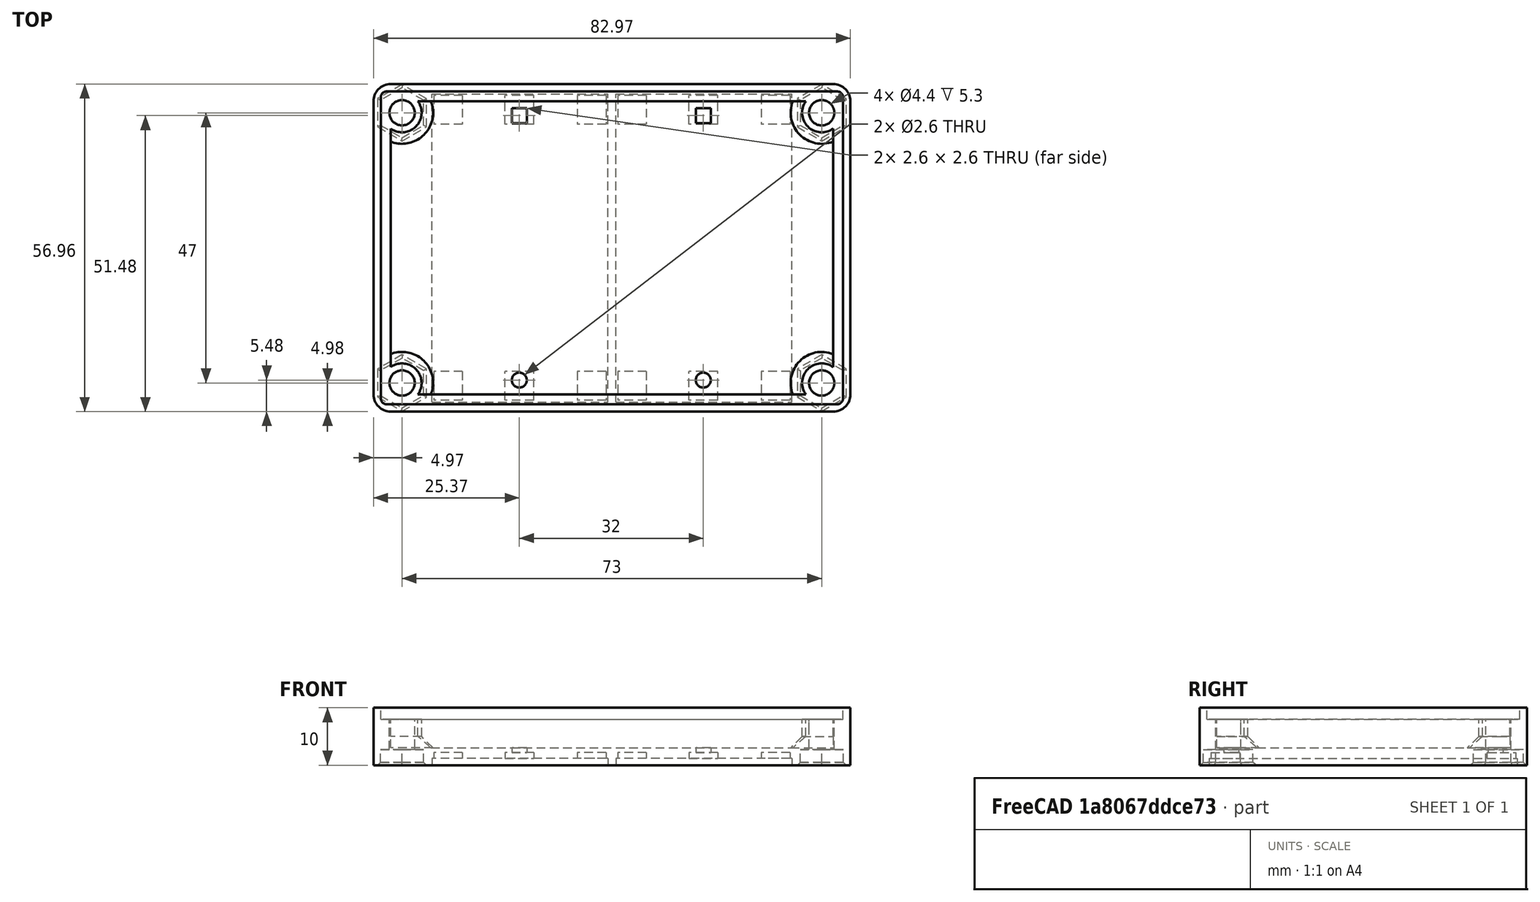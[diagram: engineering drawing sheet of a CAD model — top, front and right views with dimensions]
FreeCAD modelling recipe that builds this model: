
FCSTD DOCUMENT  (FreeCAD 0.18.4R)
Label: DoubleSolarPlate3
License: All rights reserved
LicenseURL: http://en.wikipedia.org/wiki/All_rights_reserved
objects: Part::Box×21, Part::Cylinder×14, Part::Cut×9, Part::MultiFuse×7, Sketcher::SketchObject×5, PartDesign::Pad×5, Part::Chamfer×2, Part::Fillet×1, Mesh::Feature×1
note: 69 computed .brp shape members not serialized (recipe doc carries the construction recipe); baked Part::Feature solids carry a one-line shape summary decoded from their .brp

FEATURE [Sketcher::SketchObject] Sketch002
  MapMode = 5
  sketch-geometry (8):
    g0: LineSegment StartX=7.02468 StartY=-27.9753 StartZ=0 EndX=-69.9815 EndY=-27.9753 EndZ=0
    g1: LineSegment StartX=-72.9716 StartY=-24.9853 StartZ=0 EndX=-72.9716 EndY=25.9942 EndZ=0
    g2: LineSegment StartX=-69.9853 StartY=28.9804 StartZ=0 EndX=7.02249 EndY=28.9804 EndZ=0
    g3: LineSegment StartX=10 StartY=26.0029 StartZ=0 EndX=10 EndY=-25 EndZ=0
    g4: ArcOfCircle CenterX=7.02468 CenterY=-25 CenterZ=0 NormalX=0 NormalY=0 NormalZ=1 AngleXU=0 Radius=2.97532 StartAngle=4.71239 EndAngle=6.28319
    g5: ArcOfCircle CenterX=-69.9815 CenterY=-24.9853 CenterZ=0 NormalX=0 NormalY=0 NormalZ=1 AngleXU=0 Radius=2.99005 StartAngle=3.14159 EndAngle=4.71239
    g6: ArcOfCircle CenterX=-69.9853 CenterY=25.9942 CenterZ=0 NormalX=0 NormalY=0 NormalZ=1 AngleXU=0 Radius=2.98622 StartAngle=1.5708 EndAngle=3.14159
    g7: ArcOfCircle CenterX=7.02249 CenterY=26.0029 CenterZ=0 NormalX=0 NormalY=0 NormalZ=1 AngleXU=0 Radius=2.97751 StartAngle=1.036e-13 EndAngle=1.5708
  constraints (12):
    c: Horizontal(g0)
    c: Horizontal(g2)
    c: Vertical(g1)
    c: Vertical(g3)
    c: Tangent(g3,g4) = 1.5708
    c: Tangent(g0,g4) = 1.5708
    c: Tangent(g1,g5) = 1.5708
    c: Tangent(g0,g5) = 1.5708
    c: Tangent(g1,g6) = 1.5708
    c: Tangent(g2,g6) = 1.5708
    c: Tangent(g2,g7) = 1.5708
    c: Tangent(g3,g7) = 1.5708
FEATURE [PartDesign::Pad] Pad013
  Length = 10
  Length2 = 100
  Profile = -> Sketch002
  Type = 0
FEATURE [Part::Box] Box010  label="Würfel010"
  AttacherType = Attacher::AttachEngine3D
  Height = 25
  Length = 77
  Placement = pos=(-70,-25,3) rot=(0,0,1;0rad)
  Width = 51
FEATURE [Part::Cut] Cut011
  Base = -> Pad013
  Tool = -> Box010
FEATURE [Part::Box] Box  label="Rand002"
  AttacherType = Attacher::AttachEngine3D
  Height = 2
  Length = 80.4
  Placement = pos=(-71.7,25.7,14) rot=(0,0,1;0rad)
  Width = 2
FEATURE [Part::Box] Box011  label="Rand001"
  AttacherType = Attacher::AttachEngine3D
  Height = 2
  Length = 80.4
  Placement = pos=(-71.7,-26.7,14) rot=(0,0,1;0rad)
  Width = 2
FEATURE [Part::Box] Box012  label="Rand003"
  AttacherType = Attacher::AttachEngine3D
  Height = 2
  Length = 2
  Placement = pos=(-71.7,-25,14) rot=(0,0,1;0rad)
  Width = 51
FEATURE [Part::Box] Box013  label="Rand004"
  AttacherType = Attacher::AttachEngine3D
  Height = 2
  Length = 2
  Placement = pos=(6.7,-25,14) rot=(0,0,1;0rad)
  Width = 51
FEATURE [Part::MultiFuse] Fusion  label="RandFraesung"
  Placement = pos=(0,0,-6) rot=(0,0,1;0rad)
  Shapes = -> [Box013,Box012,Box011,Box]
FEATURE [Part::Cut] Cut  label="DeckelRaw"
  Base = -> Cut011
  Tool = -> Fusion
FEATURE [Part::Cylinder] Cylinder004  label="Zylinder002"
  Angle = 360
  AttacherType = Attacher::AttachEngine3D
  Height = 8
  Radius = 3.4
FEATURE [Part::Cylinder] Cylinder  label="Zylinder001"
  Angle = 360
  AttacherType = Attacher::AttachEngine3D
  Height = 6
  Radius = 2.2
FEATURE [Part::Cut] Cut027  label="Dom001"
  Base = -> Cylinder004
  Placement = pos=(5,-23,0) rot=(0,0,1;0rad)
  Tool = -> Cylinder
FEATURE [Part::Cylinder] Cylinder015  label="Zylinder015"
  Angle = 360
  AttacherType = Attacher::AttachEngine3D
  Height = 8
  Radius = 3.4
FEATURE [Part::Cylinder] Cylinder016  label="Zylinder016"
  Angle = 360
  AttacherType = Attacher::AttachEngine3D
  Height = 10
  Radius = 2.2
FEATURE [Part::Cut] Cut028  label="Dom002"
  Base = -> Cylinder015
  Placement = pos=(-68,-23,0) rot=(0,0,1;0rad)
  Tool = -> Cylinder016
FEATURE [Part::Cylinder] Cylinder017  label="Zylinder017"
  Angle = 360
  AttacherType = Attacher::AttachEngine3D
  Height = 8
  Radius = 3.4
FEATURE [Part::Cylinder] Cylinder018  label="Zylinder018"
  Angle = 360
  AttacherType = Attacher::AttachEngine3D
  Height = 10
  Radius = 2.2
FEATURE [Part::Cut] Cut029  label="Dom003"
  Base = -> Cylinder017
  Placement = pos=(-68,24,0) rot=(0,0,1;0rad)
  Tool = -> Cylinder018
FEATURE [Part::Cylinder] Cylinder019  label="Zylinder019"
  Angle = 360
  AttacherType = Attacher::AttachEngine3D
  Height = 8
  Radius = 3.4
FEATURE [Part::Cylinder] Cylinder020  label="Zylinder020"
  Angle = 360
  AttacherType = Attacher::AttachEngine3D
  Height = 10
  Radius = 2.2
FEATURE [Part::Cut] Cut030  label="Dom004"
  Base = -> Cylinder019
  Placement = pos=(5,24,0) rot=(0,0,1;0rad)
  Tool = -> Cylinder020
FEATURE [Part::MultiFuse] Fusion001  label="DeckelMitDomen"
  Shapes = -> [Cut,Cut027,Cut028,Cut029,Cut030]
FEATURE [Part::Cylinder] Cylinder021  label="DeckelBohrung001"
  Angle = 360
  AttacherType = Attacher::AttachEngine3D
  Height = 10
  Placement = pos=(5,-23,0) rot=(0,0,1;0rad)
  Radius = 2.2
FEATURE [Part::Cylinder] Cylinder022  label="DeckelBohrung002"
  Angle = 360
  AttacherType = Attacher::AttachEngine3D
  Height = 10
  Placement = pos=(-68,-23,0) rot=(0,0,1;0rad)
  Radius = 2.2
FEATURE [Part::Cylinder] Cylinder023  label="DeckelBohrung003"
  Angle = 360
  AttacherType = Attacher::AttachEngine3D
  Height = 10
  Placement = pos=(-68,24,0) rot=(0,0,1;0rad)
  Radius = 2.2
FEATURE [Part::Cylinder] Cylinder024  label="DeckelBohrung004"
  Angle = 360
  AttacherType = Attacher::AttachEngine3D
  Height = 10
  Placement = pos=(5,24,0) rot=(0,0,1;0rad)
  Radius = 2.2
FEATURE [Part::MultiFuse] Fusion002  label="DeckelBohrungen"
  Shapes = -> [Cylinder021,Cylinder022,Cylinder023,Cylinder024]
FEATURE [Part::Cut] Cut031  label="DomeDeckelGebohrt"
  Base = -> Fusion001
  Tool = -> Fusion002
FEATURE [Sketcher::SketchObject] Sketch001
  MapMode = 5
  Placement = pos=(5,-23,0) rot=(0,0,1;0.523599rad)
  sketch-geometry (7):
    g0: LineSegment StartX=4.32745 StartY=0.001167 StartZ=0 EndX=2.16272 EndY=3.74827 EndZ=0
    g1: LineSegment StartX=2.16272 StartY=3.74827 StartZ=0 EndX=-2.16474 EndY=3.7471 EndZ=0
    g2: LineSegment StartX=-2.16474 StartY=3.7471 StartZ=0 EndX=-4.32745 EndY=-0.001167 EndZ=0
    g3: LineSegment StartX=-4.32745 StartY=-0.001167 StartZ=0 EndX=-2.16272 EndY=-3.74827 EndZ=0
    g4: LineSegment StartX=-2.16272 StartY=-3.74827 StartZ=0 EndX=2.16474 EndY=-3.7471 EndZ=0
    g5: LineSegment StartX=2.16474 StartY=-3.7471 StartZ=0 EndX=4.32745 EndY=0.001167 EndZ=0
    g6: Circle [constr] CenterX=0 CenterY=0 CenterZ=0 NormalX=0 NormalY=0 NormalZ=1 AngleXU=0 Radius=4.32745
  constraints (13):
    c: Coincident(g0,g1)
    c: Coincident(g1,g2)
    c: Coincident(g2,g3)
    c: Coincident(g3,g4)
    c: Coincident(g4,g5)
    c: Coincident(g5,g0)
    c: Equal(g0, g1-g5) x5
    c: PointOnObject(g0,g6)
    c: PointOnObject(g1,g6)
    c: PointOnObject(g2,g6)
    c: PointOnObject(g3,g6)
    c: PointOnObject(g4,g6)
    c: PointOnObject(g5,g6)
FEATURE [PartDesign::Pad] Pad  label="ScrewNut001"
  Length = 2.7
  Length2 = 100
  Placement = pos=(5,-23,0) rot=(0,0,1;0.523599rad)
  Profile = -> Sketch001
  Type = 0
FEATURE [Sketcher::SketchObject] Sketch003
  MapMode = 5
  Placement = pos=(-68,-23,0) rot=(0,0,1;0.523599rad)
  sketch-geometry (7):
    g0: LineSegment StartX=4.32745 StartY=0.001167 StartZ=0 EndX=2.16272 EndY=3.74827 EndZ=0
    g1: LineSegment StartX=2.16272 StartY=3.74827 StartZ=0 EndX=-2.16474 EndY=3.7471 EndZ=0
    g2: LineSegment StartX=-2.16474 StartY=3.7471 StartZ=0 EndX=-4.32745 EndY=-0.001167 EndZ=0
    g3: LineSegment StartX=-4.32745 StartY=-0.001167 StartZ=0 EndX=-2.16272 EndY=-3.74827 EndZ=0
    g4: LineSegment StartX=-2.16272 StartY=-3.74827 StartZ=0 EndX=2.16474 EndY=-3.7471 EndZ=0
    g5: LineSegment StartX=2.16474 StartY=-3.7471 StartZ=0 EndX=4.32745 EndY=0.001167 EndZ=0
    g6: Circle [constr] CenterX=0 CenterY=0 CenterZ=0 NormalX=0 NormalY=0 NormalZ=1 AngleXU=0 Radius=4.32745
  constraints (13):
    c: Coincident(g0,g1)
    c: Coincident(g1,g2)
    c: Coincident(g2,g3)
    c: Coincident(g3,g4)
    c: Coincident(g4,g5)
    c: Coincident(g5,g0)
    c: Equal(g0, g1-g5) x5
    c: PointOnObject(g0,g6)
    c: PointOnObject(g1,g6)
    c: PointOnObject(g2,g6)
    c: PointOnObject(g3,g6)
    c: PointOnObject(g4,g6)
    c: PointOnObject(g5,g6)
FEATURE [PartDesign::Pad] Pad014  label="ScrewNut002"
  Length = 2.7
  Length2 = 100
  Placement = pos=(-68,-23,0) rot=(0,0,1;0.523599rad)
  Profile = -> Sketch003
  Type = 0
FEATURE [Sketcher::SketchObject] Sketch004
  MapMode = 5
  Placement = pos=(-68,24,0) rot=(0,0,1;0.523599rad)
  sketch-geometry (7):
    g0: LineSegment StartX=4.32745 StartY=0.001167 StartZ=0 EndX=2.16272 EndY=3.74827 EndZ=0
    g1: LineSegment StartX=2.16272 StartY=3.74827 StartZ=0 EndX=-2.16474 EndY=3.7471 EndZ=0
    g2: LineSegment StartX=-2.16474 StartY=3.7471 StartZ=0 EndX=-4.32745 EndY=-0.001167 EndZ=0
    g3: LineSegment StartX=-4.32745 StartY=-0.001167 StartZ=0 EndX=-2.16272 EndY=-3.74827 EndZ=0
    g4: LineSegment StartX=-2.16272 StartY=-3.74827 StartZ=0 EndX=2.16474 EndY=-3.7471 EndZ=0
    g5: LineSegment StartX=2.16474 StartY=-3.7471 StartZ=0 EndX=4.32745 EndY=0.001167 EndZ=0
    g6: Circle [constr] CenterX=0 CenterY=0 CenterZ=0 NormalX=0 NormalY=0 NormalZ=1 AngleXU=0 Radius=4.32745
  constraints (13):
    c: Coincident(g0,g1)
    c: Coincident(g1,g2)
    c: Coincident(g2,g3)
    c: Coincident(g3,g4)
    c: Coincident(g4,g5)
    c: Coincident(g5,g0)
    c: Equal(g0, g1-g5) x5
    c: PointOnObject(g0,g6)
    c: PointOnObject(g1,g6)
    c: PointOnObject(g2,g6)
    c: PointOnObject(g3,g6)
    c: PointOnObject(g4,g6)
    c: PointOnObject(g5,g6)
FEATURE [PartDesign::Pad] Pad015  label="ScrewNut003"
  Length = 2.7
  Length2 = 100
  Placement = pos=(-68,24,0) rot=(0,0,1;0.523599rad)
  Profile = -> Sketch004
  Type = 0
FEATURE [Sketcher::SketchObject] Sketch005
  MapMode = 5
  Placement = pos=(5,24,0) rot=(0,0,1;0.523599rad)
  sketch-geometry (7):
    g0: LineSegment StartX=4.32745 StartY=0.001167 StartZ=0 EndX=2.16272 EndY=3.74827 EndZ=0
    g1: LineSegment StartX=2.16272 StartY=3.74827 StartZ=0 EndX=-2.16474 EndY=3.7471 EndZ=0
    g2: LineSegment StartX=-2.16474 StartY=3.7471 StartZ=0 EndX=-4.32745 EndY=-0.001167 EndZ=0
    g3: LineSegment StartX=-4.32745 StartY=-0.001167 StartZ=0 EndX=-2.16272 EndY=-3.74827 EndZ=0
    g4: LineSegment StartX=-2.16272 StartY=-3.74827 StartZ=0 EndX=2.16474 EndY=-3.7471 EndZ=0
    g5: LineSegment StartX=2.16474 StartY=-3.7471 StartZ=0 EndX=4.32745 EndY=0.001167 EndZ=0
    g6: Circle [constr] CenterX=0 CenterY=0 CenterZ=0 NormalX=0 NormalY=0 NormalZ=1 AngleXU=0 Radius=4.32745
  constraints (13):
    c: Coincident(g0,g1)
    c: Coincident(g1,g2)
    c: Coincident(g2,g3)
    c: Coincident(g3,g4)
    c: Coincident(g4,g5)
    c: Coincident(g5,g0)
    c: Equal(g0, g1-g5) x5
    c: PointOnObject(g0,g6)
    c: PointOnObject(g1,g6)
    c: PointOnObject(g2,g6)
    c: PointOnObject(g3,g6)
    c: PointOnObject(g4,g6)
    c: PointOnObject(g5,g6)
FEATURE [PartDesign::Pad] Pad016  label="ScrewNut004"
  Length = 2.7
  Length2 = 100
  Placement = pos=(5,24,0) rot=(0,0,1;0.523599rad)
  Profile = -> Sketch005
  Type = 0
FEATURE [Part::Box] Box015  label="Würfel014"
  AttacherType = Attacher::AttachEngine3D
  Height = 1.1
  Length = 5
  Placement = pos=(-15,-26,4) rot=(0,0,1;0rad)
  Width = 5
FEATURE [Part::Box] Box016  label="Würfel015"
  AttacherType = Attacher::AttachEngine3D
  Height = 1.1
  Length = 5
  Placement = pos=(10,-26,4) rot=(0,0,1;0rad)
  Width = 5
FEATURE [Part::Box] Box017  label="Würfel016"
  AttacherType = Attacher::AttachEngine3D
  Height = 1.1
  Length = 5
  Placement = pos=(-15,22,4) rot=(0,0,1;0rad)
  Width = 5
FEATURE [Part::Box] Box018  label="Würfel017"
  AttacherType = Attacher::AttachEngine3D
  Height = 1.1
  Length = 5
  Placement = pos=(10,22,4) rot=(0,0,1;0rad)
  Width = 5
FEATURE [Part::Box] Box019  label="Würfel018"
  AttacherType = Attacher::AttachEngine3D
  Height = 2
  Length = 30.6
  Placement = pos=(-15.3,-26.3,5) rot=(0,0,1;0rad)
  Width = 53.6
FEATURE [Part::Box] Box020  label="Würfel019"
  AttacherType = Attacher::AttachEngine3D
  Height = 1.1
  Length = 5
  Placement = pos=(-2.4,22,4) rot=(0,0,1;0rad)
  Width = 5
FEATURE [Part::Box] Box021  label="Würfel020"
  AttacherType = Attacher::AttachEngine3D
  Height = 1.1
  Length = 5
  Placement = pos=(-2.4,-26,4) rot=(0,0,1;0rad)
  Width = 5
FEATURE [Part::Box] Box022  label="Würfel021"
  AttacherType = Attacher::AttachEngine3D
  Height = 4.1
  Length = 2.6
  Placement = pos=(-1.2,22.2,0) rot=(0,0,1;0rad)
  Width = 2.6
FEATURE [Part::Cylinder] Cylinder025  label="Zylinder021"
  Angle = 360
  AttacherType = Attacher::AttachEngine3D
  Height = 5.1
  Placement = pos=(0.1,-22.5,0) rot=(0,0,1;0rad)
  Radius = 1.3
FEATURE [Part::MultiFuse] Fusion004  label="CellCut002"
  Placement = pos=(13,0,0) rot=(0,1,0;3.14159rad)
  Shapes = -> [Cylinder025,Box017,Box015,Box016,Box018,Box019,Box020,Box021,Box022]
FEATURE [Part::Box] Box023  label="Würfel022"
  AttacherType = Attacher::AttachEngine3D
  Height = 1.1
  Length = 5
  Placement = pos=(-15,-26,4) rot=(0,0,1;0rad)
  Width = 5
FEATURE [Part::Box] Box024  label="Würfel023"
  AttacherType = Attacher::AttachEngine3D
  Height = 1.1
  Length = 5
  Placement = pos=(10,-26,4) rot=(0,0,1;0rad)
  Width = 5
FEATURE [Part::Box] Box025  label="Würfel024"
  AttacherType = Attacher::AttachEngine3D
  Height = 1.1
  Length = 5
  Placement = pos=(-15,22,4) rot=(0,0,1;0rad)
  Width = 5
FEATURE [Part::Box] Box026  label="Würfel025"
  AttacherType = Attacher::AttachEngine3D
  Height = 1.1
  Length = 5
  Placement = pos=(10,22,4) rot=(0,0,1;0rad)
  Width = 5
FEATURE [Part::Box] Box027  label="Würfel026"
  AttacherType = Attacher::AttachEngine3D
  Height = 2
  Length = 30.6
  Placement = pos=(-15.3,-26.3,5) rot=(0,0,1;0rad)
  Width = 53.6
FEATURE [Part::Box] Box028  label="Würfel027"
  AttacherType = Attacher::AttachEngine3D
  Height = 1.1
  Length = 5
  Placement = pos=(-2.4,22,4) rot=(0,0,1;0rad)
  Width = 5
FEATURE [Part::Box] Box029  label="Würfel028"
  AttacherType = Attacher::AttachEngine3D
  Height = 1.1
  Length = 5
  Placement = pos=(-2.4,-26,4) rot=(0,0,1;0rad)
  Width = 5
FEATURE [Part::Box] Box030  label="Würfel029"
  AttacherType = Attacher::AttachEngine3D
  Height = 4.1
  Length = 2.6
  Placement = pos=(-1.2,22.2,0) rot=(0,0,1;0rad)
  Width = 2.6
FEATURE [Part::Cylinder] Cylinder026  label="Zylinder022"
  Angle = 360
  AttacherType = Attacher::AttachEngine3D
  Height = 5.1
  Placement = pos=(0.1,-22.5,0) rot=(0,0,1;0rad)
  Radius = 1.3
FEATURE [Part::MultiFuse] Fusion005  label="CellCut001"
  Placement = pos=(-19,0,0) rot=(0,1,0;3.14159rad)
  Shapes = -> [Cylinder026,Box025,Box023,Box024,Box026,Box027,Box028,Box029,Box030]
FEATURE [Part::MultiFuse] Fusion006  label="CellCut"
  Placement = pos=(-28.5,0,6.2) rot=(0,0,1;0rad)
  Shapes = -> [Fusion004,Fusion005]
FEATURE [Part::MultiFuse] Fusion007  label="ScrewNuts"
  Shapes = -> [Pad,Pad014,Pad015,Pad016]
FEATURE [Part::Cut] Cut032
  Base = -> Cut031
  Tool = -> Fusion006
FEATURE [Part::Cut] Cut033
  Base = -> Cut032
  Tool = -> Fusion007
FEATURE [Part::Chamfer] Chamfer
  Base = -> Cut033
  Edges = 24 edges r=0.5: [Edge20,Edge21,Edge22,Edge23,Edge24,Edge25,Edge26,Edge27,Edge28,Edge29,Edge30,Edge31,Edge32,Edge33,Edge34,Edge35,Edge36,Edge37,Edge38,Edge39,Edge40,Edge41,Edge42,Edge43]
FEATURE [Part::Fillet] Fillet
  Base = -> Chamfer
  Edges = 4 edges r=1: [Edge230,Edge234,Edge244,Edge246]
FEATURE [Part::Chamfer] Chamfer001
  Base = -> Fillet
  Edges = 4 edges r=2: [Edge263,Edge267,Edge268,Edge270]
FEATURE [Mesh::Feature] Mesh  label="Chamfer001 (Meshed)"
